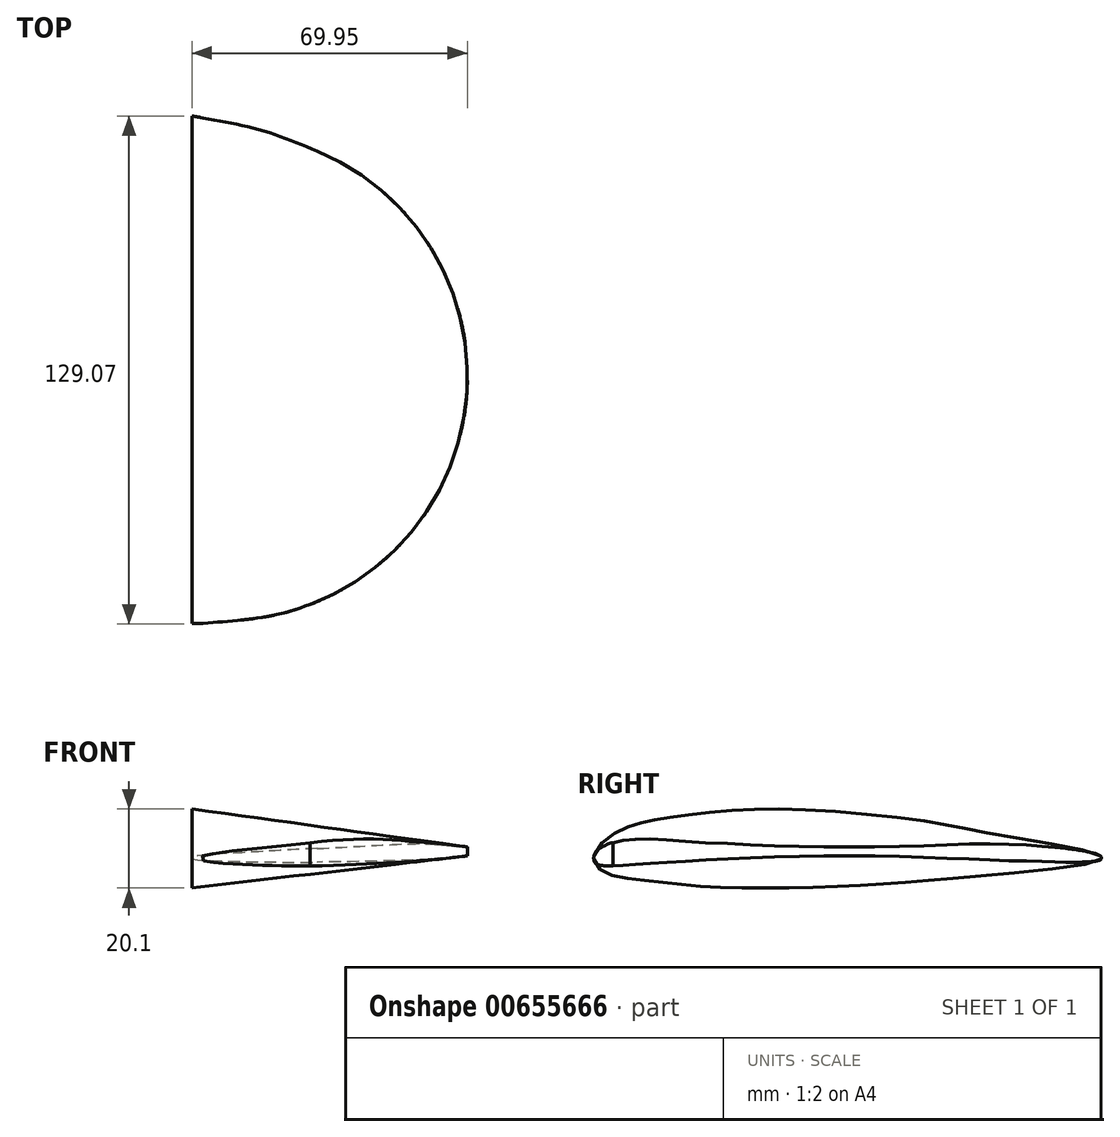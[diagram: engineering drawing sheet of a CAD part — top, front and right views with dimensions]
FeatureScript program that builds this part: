
annotation { "Feature Type Name" : "Feature", "Feature Type Description" : "" }
export const myFeature = defineFeature(function(context is Context, id is Id, definition is map)
    precondition{}
    {
        {
            var Q0;
            Q0=qCreatedBy(makeId("Top.planeOp"),FACE);
            var sketch = newSketch(context, id + "F0", { "sketchPlane" : qUnion([Q0])});
            skLineSegment(sketch, "E0", {"start": v(-320, 138.05) * mm, "end": v(-320, -155.7) * mm});
            skLineSegment(sketch, "E1", {"start": v(-320, -155.7) * mm, "end": v(325, -91.64) * mm});
            skLineSegment(sketch, "E2", {"start": v(325, -91.64) * mm, "end": v(325, 37.46) * mm});
            skLineSegment(sketch, "E3", {"start": v(325, 37.46) * mm, "end": v(-320, 138.05) * mm});
            skLineSegment(sketch, "E4", {"start": v(-95.64, -133.41) * mm, "end": v(-101.45, -252.58) * mm, "construction": true});
            skLineSegment(sketch, "E5", {"start": v(-233.28, -147.08) * mm, "end": v(-222.8, -252.58) * mm, "construction": true});
            skLineSegment(sketch, "E6", {"start": v(-124.27, -296.6) * mm, "end": v(-197.26, -296.6) * mm, "construction": true});
            skFitSpline(sketch, "E7", {"points": [v(-124.27, -296.6) * mm, v(-120.4, -294.93) * mm, v(-116.3, -292.72) * mm, v(-112.93, -288.84) * mm, v(-110.87, -284.77) * mm, v(-109.18, -280.69) * mm, v(-107.48, -275.87) * mm, v(-106.16, -272.53) * mm, v(-104.83, -266.4) * mm, v(-103.5, -262.14) * mm, v(-101.45, -252.58) * mm], "startDerivative": vector(42.21, 18) * mm, "endDerivative": vector(14.82, 77.71) * mm, "construction": true});
            skFitSpline(sketch, "E8", {"points": [v(-197.26, -296.6) * mm, v(-203.01, -295.25) * mm, v(-207.82, -291.7) * mm, v(-211.33, -287.4) * mm, v(-214.64, -281.63) * mm, v(-217.94, -275.48) * mm, v(-219.95, -269.34) * mm, v(-221.96, -262.64) * mm, v(-222.49, -258.18) * mm, v(-222.8, -252.58) * mm], "startDerivative": vector(-56.95, 5.76) * mm, "endDerivative": vector(-2.98, 54.55) * mm, "construction": true});
            skFitSpline(sketch, "E9", {"points": [v(325, -91.64) * mm, v(345.45, -89.5) * mm, v(354.96, -86.67) * mm], "startDerivative": vector(38.03, 2.68) * mm, "endDerivative": vector(20.85, 7.55) * mm});
            skFitSpline(sketch, "E10", {"points": [v(325, 37.46) * mm, v(334.83, 35.63) * mm, v(345.43, 32.92) * mm, v(356.8, 28.49) * mm], "startDerivative": vector(30.75, -5.42) * mm, "endDerivative": vector(32.5, -13.7) * mm});
            skArc(sketch, "E11", {"start": v(354.96, -86.67) * mm, "mid": v(394.94, -29.72) * mm, "end": v(356.8, 28.49) * mm});
            skArc(sketch, "E12", {"start": v(-161.45, 189.67) * mm, "mid": v(-143.5, 142.48) * mm, "end": v(-109.43, 105.21) * mm, "construction": true});
            skArc(sketch, "E13", {"start": v(-207.08, 120.44) * mm, "mid": v(-177.37, 150.5) * mm, "end": v(-161.45, 189.67) * mm, "construction": true});
            skLineSegment(sketch, "E14", {"start": v(-409.3, -166.31) * mm, "end": v(-409.3, 205.57) * mm, "construction": true});
            skLineSegment(sketch, "E15", {"start": v(539.9, 0) * mm, "end": v(-1326.82, 0) * mm, "construction": true});
            skSolve(sketch);
        }
        {
            var Q0;
            Q0=qCreatedBy(makeId("Right.planeOp"),FACE);
            cPlane(context, id + "F1", {"entities" : qUnion([Q0]), "cplaneType" : CPlaneType.OFFSET, "offset" : 320 * mm, "oppositeDirection" : true, "width" : 150 * mm, "height" : 150 * mm});
        }
        {
            var Q0;
            Q0=qCreatedBy(id+"F1.planeOp",FACE);
            var sketch = newSketch(context, id + "F2", { "sketchPlane" : qUnion([Q0])});
            skPoint(sketch, "E16", {"position": v(-155.73, 0.05) * mm});
            skPoint(sketch, "E17", {"position": v(146.43, 0.05) * mm});
            skPoint(sketch, "E18", {"position": v(-140.82, 16.95) * mm});
            skPoint(sketch, "E19", {"position": v(-113.5, 27.88) * mm});
            skPoint(sketch, "E20", {"position": v(-81.18, 31.58) * mm});
            skPoint(sketch, "E21", {"position": v(-35.84, 31.58) * mm});
            skPoint(sketch, "E22", {"position": v(9.51, 26.86) * mm});
            skPoint(sketch, "E23", {"position": v(41.81, 22.5) * mm});
            skPoint(sketch, "E24", {"position": v(91.59, 12.93) * mm});
            skPoint(sketch, "E25", {"position": v(101.43, -4.3) * mm});
            skPoint(sketch, "E26", {"position": v(54.69, -9.04) * mm});
            skPoint(sketch, "E27", {"position": v(1.98, -13.78) * mm});
            skPoint(sketch, "E28", {"position": v(-40.54, -16.77) * mm});
            skPoint(sketch, "E29", {"position": v(-83.94, -18.17) * mm});
            skPoint(sketch, "E30", {"position": v(-136.66, -13.96) * mm});
            skPoint(sketch, "E31", {"position": v(-110.13, -17.47) * mm});
            skFitSpline(sketch, "E32", {"points": [v(146.43, 0.05) * mm, v(91.59, 12.93) * mm, v(41.81, 22.5) * mm, v(9.51, 26.86) * mm, v(-35.84, 31.58) * mm, v(-81.18, 31.58) * mm, v(-113.5, 27.88) * mm, v(-140.82, 16.95) * mm, v(-155.73, 0.05) * mm, v(-151.76, -9.02) * mm, v(-136.66, -13.96) * mm, v(-110.13, -17.47) * mm, v(-83.94, -18.17) * mm, v(-40.54, -16.77) * mm, v(1.98, -13.78) * mm, v(54.69, -9.04) * mm, v(101.43, -4.3) * mm, v(146.43, 0.05) * mm]});
            skLineSegment(sketch, "E33.0", {"start": v(138.05, 0) * mm, "end": v(-155.7, 0) * mm, "construction": true});
            skSolve(sketch);
        }
        {
            var Q0;
            Q0=qCreatedBy(makeId("Right.planeOp"),FACE);
            cPlane(context, id + "F3", {"entities" : qUnion([Q0]), "cplaneType" : CPlaneType.OFFSET, "offset" : 325 * mm, "width" : 150 * mm, "height" : 150 * mm});
        }
        {
            var Q0;
            Q0=qCreatedBy(id+"F3.planeOp",FACE);
            var sketch = newSketch(context, id + "F4", { "sketchPlane" : qUnion([Q0])});
            skPoint(sketch, "E34", {"position": v(-89.07, 14) * mm});
            skPoint(sketch, "E35", {"position": v(-82.28, 12.18) * mm});
            skPoint(sketch, "E36", {"position": v(-71.85, 10.96) * mm});
            skPoint(sketch, "E37", {"position": v(-60.32, 10) * mm});
            skPoint(sketch, "E38", {"position": v(-44.43, 9.87) * mm});
            skPoint(sketch, "E39", {"position": v(-26.1, 10.36) * mm});
            skPoint(sketch, "E40", {"position": v(-9.97, 11.45) * mm});
            skPoint(sketch, "E41", {"position": v(13.57, 13.51) * mm});
            skPoint(sketch, "E42", {"position": v(-87.01, 23.22) * mm});
            skPoint(sketch, "E43", {"position": v(-72.94, 27.59) * mm});
            skPoint(sketch, "E44", {"position": v(-58.14, 29.4) * mm});
            skPoint(sketch, "E45", {"position": v(-36.42, 29.65) * mm});
            skPoint(sketch, "E46", {"position": v(-5.48, 26.5) * mm});
            skPoint(sketch, "E47", {"position": v(11.26, 23.34) * mm});
            skPoint(sketch, "E48", {"position": v(-80.1, 26.25) * mm});
            skFitSpline(sketch, "E49", {"points": [v(37.6, 17.55) * mm, v(11.26, 23.34) * mm, v(-5.48, 26.5) * mm, v(-36.42, 29.65) * mm, v(-58.14, 29.4) * mm, v(-72.94, 27.59) * mm, v(-80.1, 26.25) * mm, v(-87.01, 23.22) * mm, v(-91.5, 17.55) * mm, v(-89.07, 14) * mm, v(-82.28, 12.18) * mm, v(-71.85, 10.96) * mm, v(-60.32, 10) * mm, v(-44.43, 9.87) * mm, v(-26.1, 10.36) * mm, v(-9.97, 11.45) * mm, v(13.57, 13.51) * mm, v(37.6, 17.55) * mm]});
            skSolve(sketch);
        }
        {
            var Q0;
            Q0 = qSketchRegion(id + "F2", true);
            var Q1;
            Q1 = qSketchRegion(id + "F4", true);
            loft(context, id + "F5", {"sheetProfilesArray" : [{ "sheetProfileEntities" : qUnion([Q0]) }, { "sheetProfileEntities" : qUnion([Q1]) }]});
        }
        {
            var Q0;
            Q0=makeQuery(id+"F5.opLoft","CAP_FACE",FACE,{"disambiguationData":[OSD([makeQuery(id+"F2.imprint","IMPRINT",FACE,{"disambiguationData":[TD([[makeQuery(id+"F2.imprint","IMPRINT",EDGE,{"derivedFrom":sQuery(id+"F2.wireOp",EDGE,"E32")}),1.0]])]})])],"isStart":true});
            var sketch = newSketch(context, id + "F6", { "sketchPlane" : qUnion([Q0])});
            skCircle(sketch, "E50", {"center": v(116.58, 5.83) * mm, "radius": 5 * mm});
            skSolve(sketch);
        }
        {
            var Q0;
            Q0=makeQuery(id+"F5.opLoft","CAP_FACE",FACE,{"disambiguationData":[OSD([makeQuery(id+"F4.imprint","IMPRINT",FACE,{"disambiguationData":[TD([[makeQuery(id+"F4.imprint","IMPRINT",EDGE,{"derivedFrom":sQuery(id+"F4.wireOp",EDGE,"E49")}),1.0]])]})])],"isStart":true});
            var sketch = newSketch(context, id + "F7", { "sketchPlane" : qUnion([Q0])});
            skCircle(sketch, "E51", {"center": v(-65.52, 19.37) * mm, "radius": 5 * mm});
            skSolve(sketch);
        }
        {
            var Q0;
            Q0=qCreatedBy(id+"F3.planeOp",FACE);
            cPlane(context, id + "F8", {"entities" : qUnion([Q0]), "cplaneType" : CPlaneType.OFFSET, "offset" : 70 * mm, "width" : 150 * mm, "height" : 150 * mm});
        }
        {
            var Q0;
            Q0=qCreatedBy(id+"F8.planeOp",FACE);
            var sketch = newSketch(context, id + "F9", { "sketchPlane" : qUnion([Q0])});
            skPoint(sketch, "E52", {"position": v(-91.61, 18) * mm});
            skPoint(sketch, "E53", {"position": v(-81.05, 20.22) * mm});
            skPoint(sketch, "E54", {"position": v(-58.26, 20.22) * mm});
            skPoint(sketch, "E55", {"position": v(-45.76, 20.22) * mm});
            skPoint(sketch, "E56", {"position": v(-25.2, 20.22) * mm});
            skPoint(sketch, "E57", {"position": v(-4.35, 20.22) * mm});
            skPoint(sketch, "E58", {"position": v(15.65, 20.22) * mm});
            skPoint(sketch, "E59", {"position": v(37.05, 18) * mm});
            skPoint(sketch, "E60", {"position": v(13.99, 18) * mm});
            skPoint(sketch, "E61", {"position": v(-5.19, 18) * mm});
            skPoint(sketch, "E62", {"position": v(-25.2, 18) * mm});
            skPoint(sketch, "E63", {"position": v(-46.04, 18) * mm});
            skPoint(sketch, "E64", {"position": v(-57.99, 18) * mm});
            skPoint(sketch, "E65", {"position": v(-81.05, 18) * mm});
            skPoint(sketch, "E66", {"position": v(25.66, 18) * mm});
            skPoint(sketch, "E67", {"position": v(-67.16, 18) * mm});
            skPoint(sketch, "E68", {"position": v(-67.44, 20.22) * mm});
            skFitSpline(sketch, "E69", {"points": [v(-91.61, 18) * mm, v(-81.05, 20.22) * mm, v(-67.44, 20.22) * mm, v(-58.26, 20.22) * mm, v(-45.76, 20.22) * mm, v(-25.2, 20.22) * mm, v(-4.35, 20.22) * mm, v(15.65, 20.22) * mm, v(37.05, 18) * mm, v(25.66, 18) * mm, v(13.99, 18) * mm, v(-5.19, 18) * mm, v(-25.2, 18) * mm, v(-46.04, 18) * mm, v(-57.99, 18) * mm, v(-67.16, 18) * mm, v(-81.05, 18) * mm, v(-91.61, 18) * mm]});
            skSolve(sketch);
        }
        {
            var Q0;
            Q0 = qSketchRegion(id + "F4", true);
            var Q1;
            Q1 = qSketchRegion(id + "F9", true);
            loft(context, id + "F10", {"sheetProfilesArray" : [{ "sheetProfileEntities" : qUnion([Q0]) }, { "sheetProfileEntities" : qUnion([Q1]) }]});
        }
        {
            var Q0;
            Q0 = qSketchRegion(id + "F6", true);
            var Q1;
            Q1 = qSketchRegion(id + "F7", true);
            loft(context, id + "F11", {"operationType" : NewBodyOperationType.REMOVE, "sheetProfilesArray" : [{ "sheetProfileEntities" : qUnion([Q0]) }, { "sheetProfileEntities" : qUnion([Q1]) }]});
        }
        {
            var Q0;
            Q0=makeQuery(id+"F5.opLoft","CAP_FACE",FACE,{"disambiguationData":[OSD([makeQuery(id+"F2.imprint","IMPRINT",FACE,{"disambiguationData":[TD([[makeQuery(id+"F2.imprint","IMPRINT",EDGE,{"derivedFrom":sQuery(id+"F2.wireOp",EDGE,"E32")}),1.0]])]})])],"isStart":true});
            var sketch = newSketch(context, id + "F12", { "sketchPlane" : qUnion([Q0])});
            skArc(sketch, "E70", {"start": v(-51.01, 7.26) * mm, "mid": v(-54.71, 2.27) * mm, "end": v(-50.7, -2.48) * mm});
            skArc(sketch, "E71", {"start": v(-50.7, -2.48) * mm, "mid": v(-44.72, 2.59) * mm, "end": v(-51.01, 7.26) * mm});
            skSolve(sketch);
        }
        {
            var Q0;
            Q0=makeQuery(id+"F5.opLoft","CAP_FACE",FACE,{"disambiguationData":[OSD([makeQuery(id+"F4.imprint","IMPRINT",FACE,{"disambiguationData":[TD([[makeQuery(id+"F4.imprint","IMPRINT",EDGE,{"derivedFrom":sQuery(id+"F4.wireOp",EDGE,"E49")}),1.0]])]})])],"isStart":true});
            var sketch = newSketch(context, id + "F13", { "sketchPlane" : qUnion([Q0])});
            skArc(sketch, "E72", {"start": v(-3.78, 24.03) * mm, "mid": v(-9.68, 18.5) * mm, "end": v(-2.62, 14.58) * mm});
            skArc(sketch, "E73", {"start": v(-2.62, 14.58) * mm, "mid": v(0.24, 19.72) * mm, "end": v(-3.78, 24.03) * mm});
            skSolve(sketch);
        }
        {
            var Q0;
            Q0 = qSketchRegion(id + "F12", true);
            var Q1;
            Q1 = qSketchRegion(id + "F13", true);
            var Q2;
            Q2=sQuery(id+"F13.wireOp",VERTEX,"E73.end");
            var Q3;
            Q3=sQuery(id+"F12.wireOp",VERTEX,"E70.start");
            loft(context, id + "F14", {"operationType" : NewBodyOperationType.REMOVE, "sheetProfilesArray" : [{ "sheetProfileEntities" : qUnion([Q0]) }, { "sheetProfileEntities" : qUnion([Q1]) }], "matchConnections" : true, "connections" : [{ "connectionEntities" : qUnion([Q2, Q3]), "connectionEdgeQueries" : qUnion([]), "connectionEdgeParameters" : [] }]});
        }
        {
            var Q0;
            Q0=makeQuery(id+"F0.imprint","IMPRINT",FACE,{"disambiguationData":[TD([[makeQuery(id+"F0.imprint","IMPRINT",EDGE,{"derivedFrom":sQuery(id+"F0.wireOp",EDGE,"E2")}),-1.0]])]});
            extrude(context, id + "F15", {"entities" : qUnion([Q0]), "operationType" : NewBodyOperationType.INTERSECT, "endBound" : BoundingType.THROUGH_ALL, "depth" : 52.8 * mm, "offsetDistance" : 25 * mm});
        }
    });
